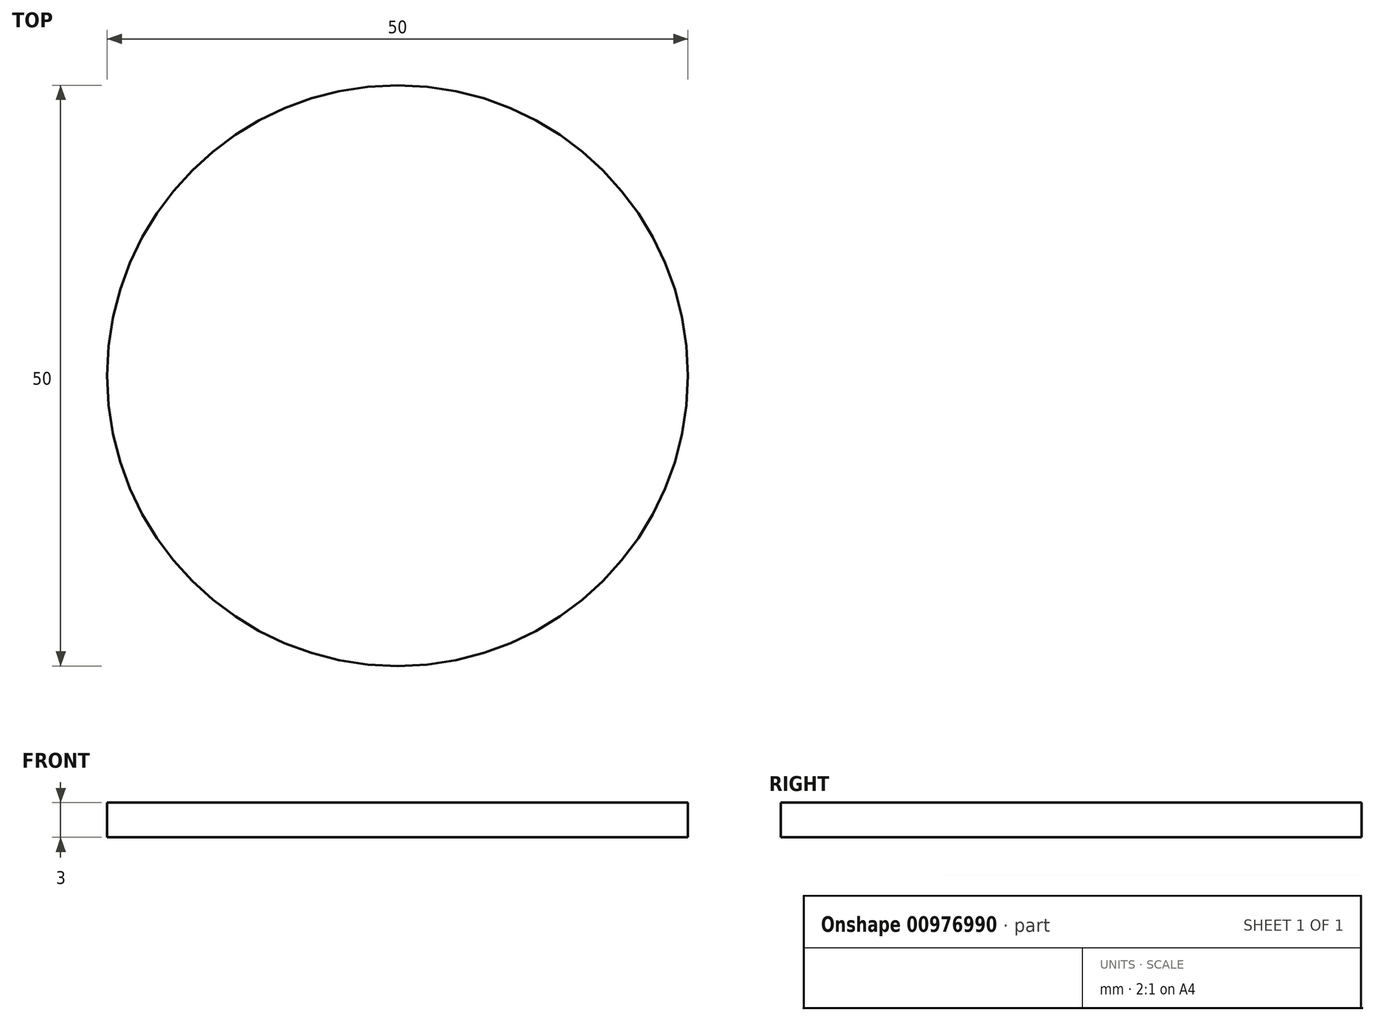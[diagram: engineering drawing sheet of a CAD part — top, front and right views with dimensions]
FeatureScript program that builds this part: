
annotation { "Feature Type Name" : "Feature", "Feature Type Description" : "" }
export const myFeature = defineFeature(function(context is Context, id is Id, definition is map)
    precondition{}
    {
        {
            var Q0;
            Q0=qCreatedBy(makeId("Top.planeOp"),FACE);
            var sketch = newSketch(context, id + "F0", { "sketchPlane" : qUnion([Q0])});
            skCircle(sketch, "E0", {"center": v(0, 0) * mm, "radius": 25 * mm});
            skSolve(sketch);
        }
        {
            var Q0;
            Q0=makeQuery(id+"F0.imprint","IMPRINT",FACE,{"disambiguationData":[TD([[makeQuery(id+"F0.imprint","IMPRINT",EDGE,{"derivedFrom":sQuery(id+"F0.wireOp",EDGE,"E0")}),1.0]])]});
            extrude(context, id + "F1", {"entities" : qUnion([Q0]), "depth" : 3 * mm, "offsetDistance" : 25 * mm});
        }
    });
